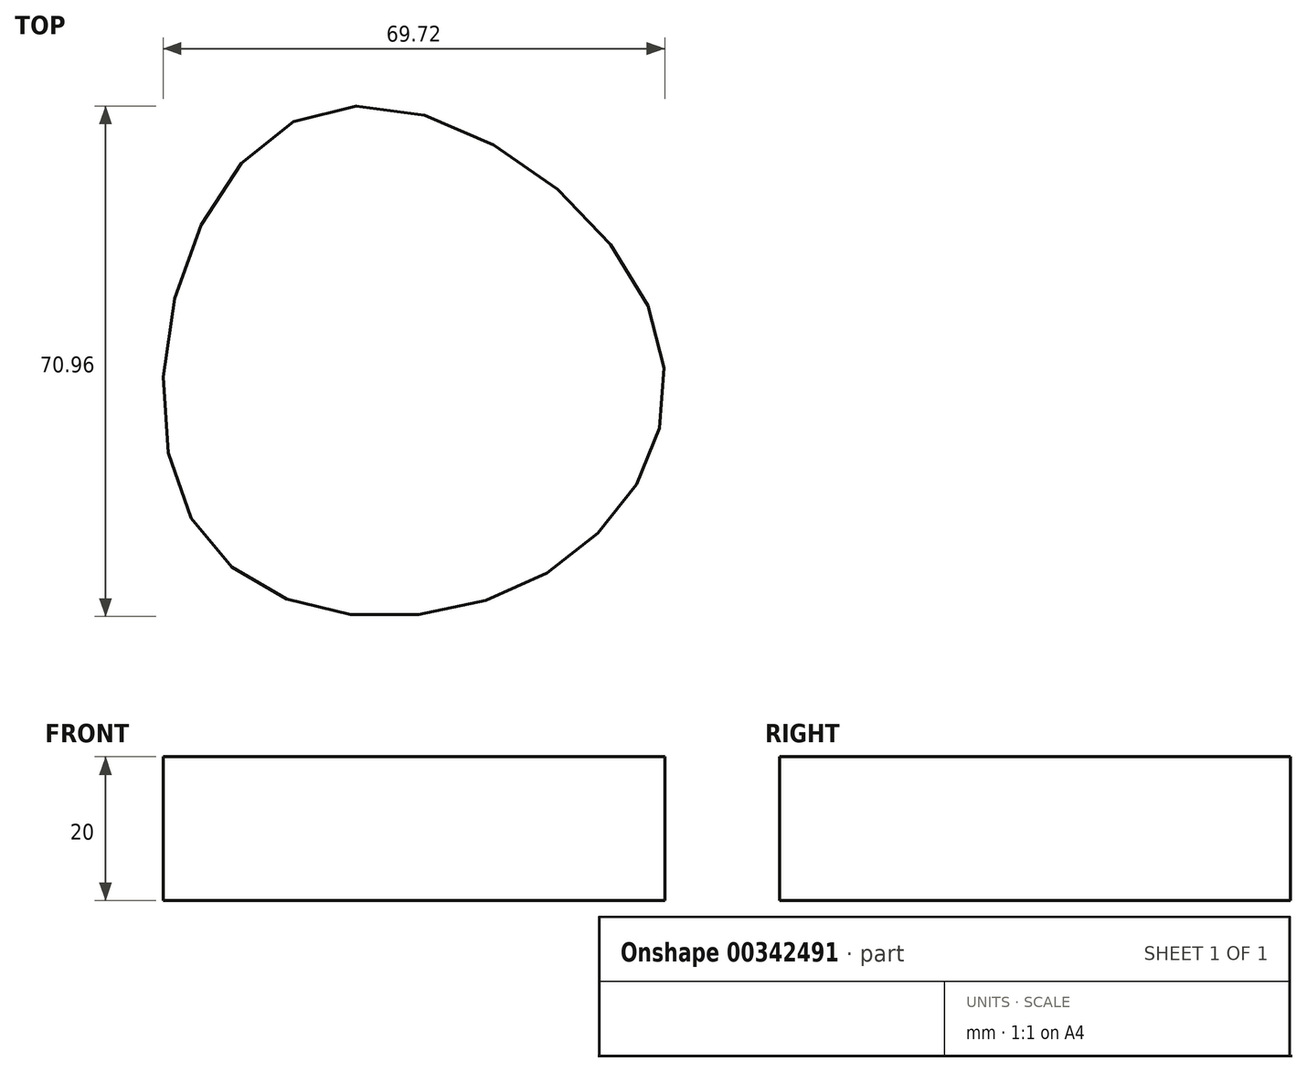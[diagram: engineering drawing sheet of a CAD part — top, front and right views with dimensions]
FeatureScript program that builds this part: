
annotation { "Feature Type Name" : "Feature", "Feature Type Description" : "" }
export const myFeature = defineFeature(function(context is Context, id is Id, definition is map)
    precondition{}
    {
        {
            var Q0;
            Q0=qCreatedBy(makeId("Top.planeOp"),FACE);
            var sketch = newSketch(context, id + "F0", { "sketchPlane" : qUnion([Q0])});
            skFitSpline(sketch, "E0", {"points": [v(-134.64, -58.72) * mm, v(-119.05, -2.96) * mm, v(-70.3, -31.33) * mm, v(-89, -68.35) * mm, v(-134.64, -58.72) * mm]});
            skSolve(sketch);
        }
        {
            var Q0;
            Q0=makeQuery(id+"F0.imprint","IMPRINT",FACE,{"disambiguationData":[TD([[makeQuery(id+"F0.imprint","IMPRINT",EDGE,{"derivedFrom":sQuery(id+"F0.wireOp",EDGE,"E0")}),-1.0]])]});
            extrude(context, id + "F1", {"entities" : qUnion([Q0]), "depth" : 20 * mm});
        }
    });
